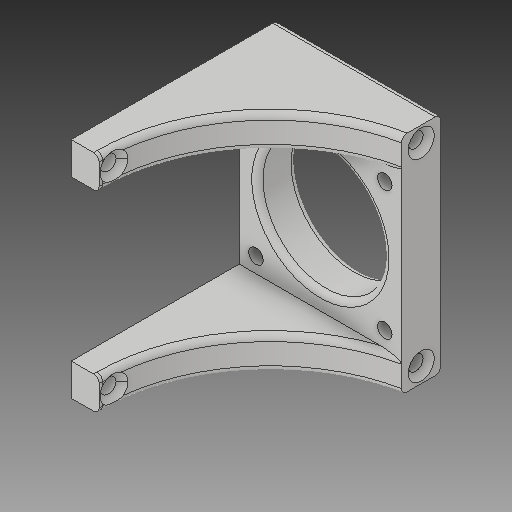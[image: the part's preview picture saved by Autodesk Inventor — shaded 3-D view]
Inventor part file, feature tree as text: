
AUTODESK INVENTOR PART (.ipt)
format: ipt  version: 2019 (Build 230136000, 136)  size: 285,184 bytes
history: native  units: mm
features: other x3, sketch x3
ambient origin geometry x8: Origin, YZ Plane, XZ Plane, XY Plane, X Axis, Y Axis, Z Axis, Center Point
bodies: Solid1 (feature_tree)
feature tree (6):
  other  "Nema11_holder.ipt"
  other  "Solid1::Nema11_holder.ipt"
  other  "TaggingFeature1"
  sketch  "Sketch1"  dims[d0=10.0mm]
  sketch  "Sketch2"
  sketch  "Sketch3"
